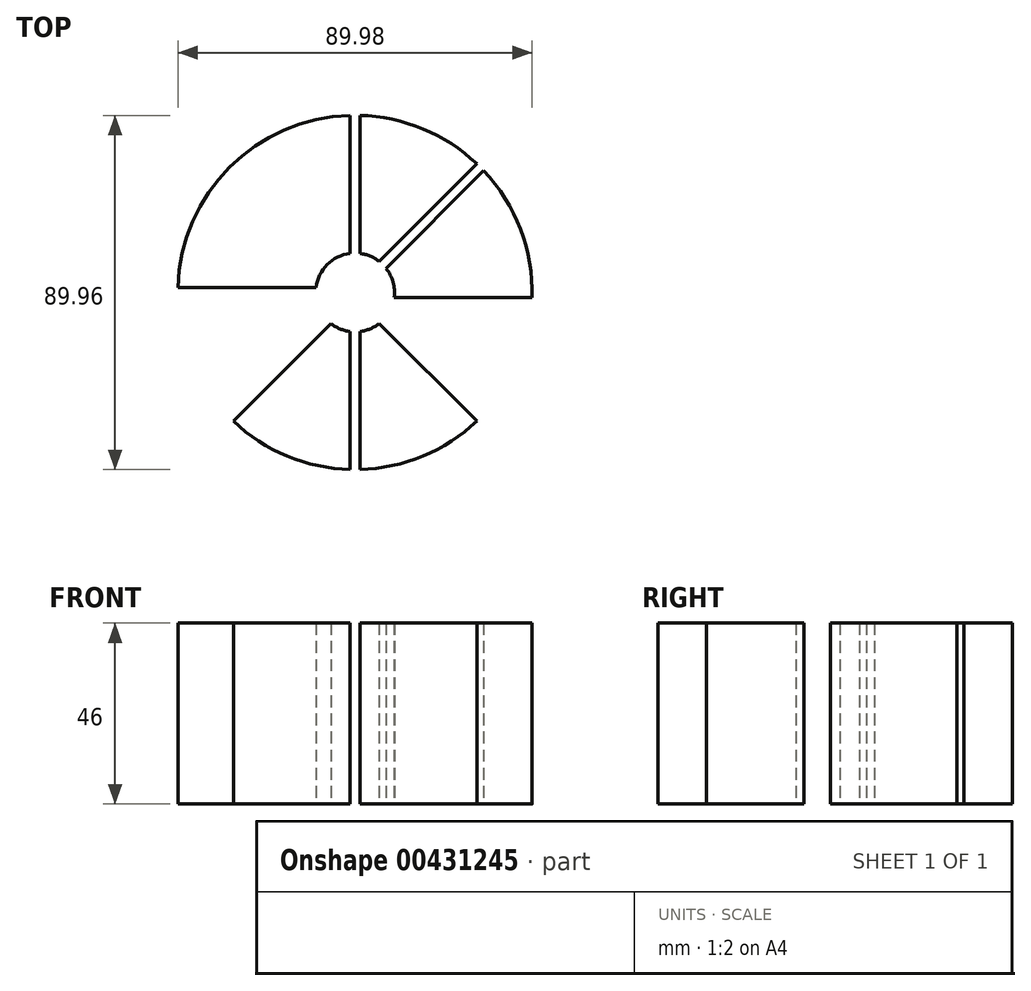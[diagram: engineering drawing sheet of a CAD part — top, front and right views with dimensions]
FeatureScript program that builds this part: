
annotation { "Feature Type Name" : "Feature", "Feature Type Description" : "" }
export const myFeature = defineFeature(function(context is Context, id is Id, definition is map)
    precondition{}
    {
        {
            var Q0;
            Q0=qCreatedBy(makeId("Top.planeOp"),FACE);
            var sketch = newSketch(context, id + "F0", { "sketchPlane" : qUnion([Q0])});
            skCircle(sketch, "E0", {"center": v(0, 0) * mm, "radius": 45 * mm});
            skCircle(sketch, "E1", {"center": v(0, 0) * mm, "radius": 10 * mm});
            skLineSegment(sketch, "E2.bottom", {"start": v(1.25, 56.98) * mm, "end": v(-1.25, 56.98) * mm});
            skLineSegment(sketch, "E2.top", {"start": v(1.25, -56.98) * mm, "end": v(-1.25, -56.98) * mm});
            skLineSegment(sketch, "E2.left", {"start": v(1.25, 56.98) * mm, "end": v(1.25, -56.98) * mm});
            skLineSegment(sketch, "E2.right", {"start": v(-1.25, 56.98) * mm, "end": v(-1.25, -56.98) * mm});
            skLineSegment(sketch, "E3.1.0", {"start": v(41.17, 39.4) * mm, "end": v(-39.4, -41.17) * mm});
            skLineSegment(sketch, "E3.1.1", {"start": v(39.4, 41.17) * mm, "end": v(-41.17, -39.4) * mm});
            skLineSegment(sketch, "E3.1.2", {"start": v(41.17, 39.4) * mm, "end": v(39.4, 41.17) * mm});
            skLineSegment(sketch, "E3.1.3", {"start": v(-39.4, -41.17) * mm, "end": v(-41.17, -39.4) * mm});
            skLineSegment(sketch, "E3.2.0", {"start": v(56.98, -1.25) * mm, "end": v(-56.98, -1.25) * mm});
            skLineSegment(sketch, "E3.2.1", {"start": v(56.98, 1.25) * mm, "end": v(-56.98, 1.25) * mm});
            skLineSegment(sketch, "E3.2.2", {"start": v(56.98, -1.25) * mm, "end": v(56.98, 1.25) * mm});
            skLineSegment(sketch, "E3.2.3", {"start": v(-56.98, -1.25) * mm, "end": v(-56.98, 1.25) * mm});
            skLineSegment(sketch, "E3.3.0", {"start": v(39.4, -41.17) * mm, "end": v(-41.17, 39.4) * mm});
            skLineSegment(sketch, "E3.3.1", {"start": v(41.17, -39.4) * mm, "end": v(-39.4, 41.17) * mm});
            skLineSegment(sketch, "E3.3.2", {"start": v(39.4, -41.17) * mm, "end": v(41.17, -39.4) * mm});
            skLineSegment(sketch, "E3.3.3", {"start": v(-41.17, 39.4) * mm, "end": v(-39.4, 41.17) * mm});
            skLineSegment(sketch, "E3.anchor1", {"start": v(0, 0) * mm, "end": v(-1.25, -56.98) * mm, "construction": true});
            skLineSegment(sketch, "E3.anchor2", {"start": v(0, 0) * mm, "end": v(-39.4, 41.17) * mm, "construction": true});
            skSolve(sketch);
        }
        {
            var Q0;
            {var subQ0=sQuery(id+"F0.wireOp",EDGE,"E2.right");var subQ1=sQuery(id+"F0.wireOp",EDGE,"E0");var subQ2=makeQuery(id+"F0.imprint","INTERSECT",VERTEX,{"disambiguationData":[OD(0.0)],"derivedFrom":[subQ1,subQ0]});Q0=makeQuery(id+"F0.imprint","IMPRINT",FACE,{"disambiguationData":[TD([[makeQuery(id+"F0.imprint","IMPRINT",EDGE,{"disambiguationData":[TD([[subQ2,-1.0]])],"derivedFrom":subQ1}),1.0]])]});}
            var Q1;
            {var subQ0=sQuery(id+"F0.wireOp",EDGE,"E3.3.0");var subQ1=sQuery(id+"F0.wireOp",EDGE,"E0");var subQ2=makeQuery(id+"F0.imprint","INTERSECT",VERTEX,{"disambiguationData":[OD(0.0)],"derivedFrom":[subQ1,subQ0]});Q1=makeQuery(id+"F0.imprint","IMPRINT",FACE,{"disambiguationData":[TD([[makeQuery(id+"F0.imprint","IMPRINT",EDGE,{"disambiguationData":[TD([[subQ2,-1.0]])],"derivedFrom":subQ1}),1.0]])]});}
            var Q2;
            {var subQ0=sQuery(id+"F0.wireOp",EDGE,"E3.2.0");var subQ1=sQuery(id+"F0.wireOp",EDGE,"E0");var subQ2=makeQuery(id+"F0.imprint","INTERSECT",VERTEX,{"disambiguationData":[OD(0.0)],"derivedFrom":[subQ1,subQ0]});Q2=makeQuery(id+"F0.imprint","IMPRINT",FACE,{"disambiguationData":[TD([[makeQuery(id+"F0.imprint","IMPRINT",EDGE,{"disambiguationData":[TD([[subQ2,-1.0]])],"derivedFrom":subQ1}),1.0]])]});}
            var Q3;
            {var subQ0=sQuery(id+"F0.wireOp",EDGE,"E3.1.0");var subQ1=sQuery(id+"F0.wireOp",EDGE,"E0");var subQ2=makeQuery(id+"F0.imprint","INTERSECT",VERTEX,{"disambiguationData":[OD(1.0)],"derivedFrom":[subQ1,subQ0]});Q3=makeQuery(id+"F0.imprint","IMPRINT",FACE,{"disambiguationData":[TD([[makeQuery(id+"F0.imprint","IMPRINT",EDGE,{"disambiguationData":[TD([[subQ2,-1.0]])],"derivedFrom":subQ1}),1.0]])]});}
            var Q4;
            {var subQ0=sQuery(id+"F0.wireOp",EDGE,"E2.left");var subQ1=sQuery(id+"F0.wireOp",EDGE,"E0");var subQ2=makeQuery(id+"F0.imprint","INTERSECT",VERTEX,{"disambiguationData":[OD(1.0)],"derivedFrom":[subQ1,subQ0]});Q4=makeQuery(id+"F0.imprint","IMPRINT",FACE,{"disambiguationData":[TD([[makeQuery(id+"F0.imprint","IMPRINT",EDGE,{"disambiguationData":[TD([[subQ2,-1.0]])],"derivedFrom":subQ1}),1.0]])]});}
            var Q5;
            {var subQ0=sQuery(id+"F0.wireOp",EDGE,"E3.3.1");var subQ1=sQuery(id+"F0.wireOp",EDGE,"E0");var subQ2=makeQuery(id+"F0.imprint","INTERSECT",VERTEX,{"disambiguationData":[OD(1.0)],"derivedFrom":[subQ1,subQ0]});Q5=makeQuery(id+"F0.imprint","IMPRINT",FACE,{"disambiguationData":[TD([[makeQuery(id+"F0.imprint","IMPRINT",EDGE,{"disambiguationData":[TD([[subQ2,-1.0]])],"derivedFrom":subQ1}),1.0]])]});}
            var Q6;
            {var subQ0=sQuery(id+"F0.wireOp",EDGE,"E3.1.0");var subQ1=sQuery(id+"F0.wireOp",EDGE,"E0");var subQ2=makeQuery(id+"F0.imprint","INTERSECT",VERTEX,{"disambiguationData":[OD(0.0)],"derivedFrom":[subQ1,subQ0]});Q6=makeQuery(id+"F0.imprint","IMPRINT",FACE,{"disambiguationData":[TD([[makeQuery(id+"F0.imprint","IMPRINT",EDGE,{"disambiguationData":[TD([[subQ2,1.0]])],"derivedFrom":subQ1}),1.0]])]});}
            var Q7;
            {var subQ0=sQuery(id+"F0.wireOp",EDGE,"E3.1.1");var subQ1=sQuery(id+"F0.wireOp",EDGE,"E0");var subQ2=makeQuery(id+"F0.imprint","INTERSECT",VERTEX,{"disambiguationData":[OD(0.0)],"derivedFrom":[subQ1,subQ0]});Q7=makeQuery(id+"F0.imprint","IMPRINT",FACE,{"disambiguationData":[TD([[makeQuery(id+"F0.imprint","IMPRINT",EDGE,{"disambiguationData":[TD([[subQ2,-1.0]])],"derivedFrom":subQ1}),1.0]])]});}
            extrude(context, id + "F1", {"entities" : qUnion([Q0, Q1, Q2, Q3, Q4, Q5, Q6, Q7]), "depth" : 46 * mm});
        }
    });
